# Revit family: Sink-Undermount-Bar-KOHLER-Northland-K-6589
name_source: partatom
category: Plumbing Fixtures
units: mm (PartAtom-declared; Revit-internal decimal feet)

## family parameters
Cut with Voids When Loaded = No
Host = Face
Maintain Annotation Orientation = No
OmniClass Number = 23.31.13.00
OmniClass Title = Sinks
Part Type = Normal
Room Calculation Point = No
Round Connector Dimension = Use Diameter
Shared = No

## types (10) — shared parameters
ADA Compliant = No
Assembly Code = D2010400
CW Connection = No
Cold Water Inlet = Cold Water Inlet
Date Modified = 05/30/2025
Default Elevation = 36"
Description = 15 Inch Undermount Single-Bowl Bar Sink
Drain Included = No
HW Connection = No
Height = 10"
Hot Water Inlet = Hot Water Inlet
Length = 15"
Manufacturer = Kohler Co.
Master Format 2014 = 22 41 16
Master Format 2014 Name = Residential Lavatories and Sinks
Material = Enameled Cast Iron
Product Documentation Link = https://www.us.kohler.com
Product Name = Northland
Product Page URL = http://www.us.kohler.com
URL = https://www.us.kohler.com
Vent Connection = No
Waste Connection = Yes
Waste Water Outlet = Waste Water Outlet
WaterSense Certified = No
Width = 12 5/16"

## per-type parameters (varying)
| type | Finish | Model | Type |
| 0-White | KOHLER-Enameled_Cast_Iron-0-White | K-6589-U-0 | 1 |
| 58-Thunder Grey | KOHLER-Enameled_Cast_Iron-58-Thunder_Grey | K-6589-U-58 | 2 |
| 7-Black Black | KOHLER-Enameled_Cast_Iron-7-Black_Black | K-6589-U-7 | 3 |
| 95-Ice Grey | KOHLER-Enameled_Cast_Iron-95-Ice_Grey | K-6589-U-95 | 4 |
| 96-Biscuit | KOHLER-Enameled_Cast_Iron-96-Biscuit | K-6589-U-96 | 5 |
| FF-Sea Salt | KOHLER-Enameled_Cast_Iron-FF-Sea_Salt | K-6589-U-FF | 6 |
| TRF-Truffle | KOHLER-Enameled_Cast_Iron-TRF-Truffle | K-6589-U-TRF | 7 |
| 17-Teal | KOHLER-Enameled_Cast_Iron-17-Teal | K-6589-U-17 | 8 |
| 34-Fresh Green | KOHLER-Enameled_Cast_Iron-34-Fresh_Green | K-6589-U-34 | 9 |
| 42-Aspen Green | KOHLER-Enameled_Cast_Iron-42-Aspen_Green | K-6589-U-42 | 10 |

## geometry (parser evidence)
native form markers: Sweep x5
no freeform markers — native parametric forms only
